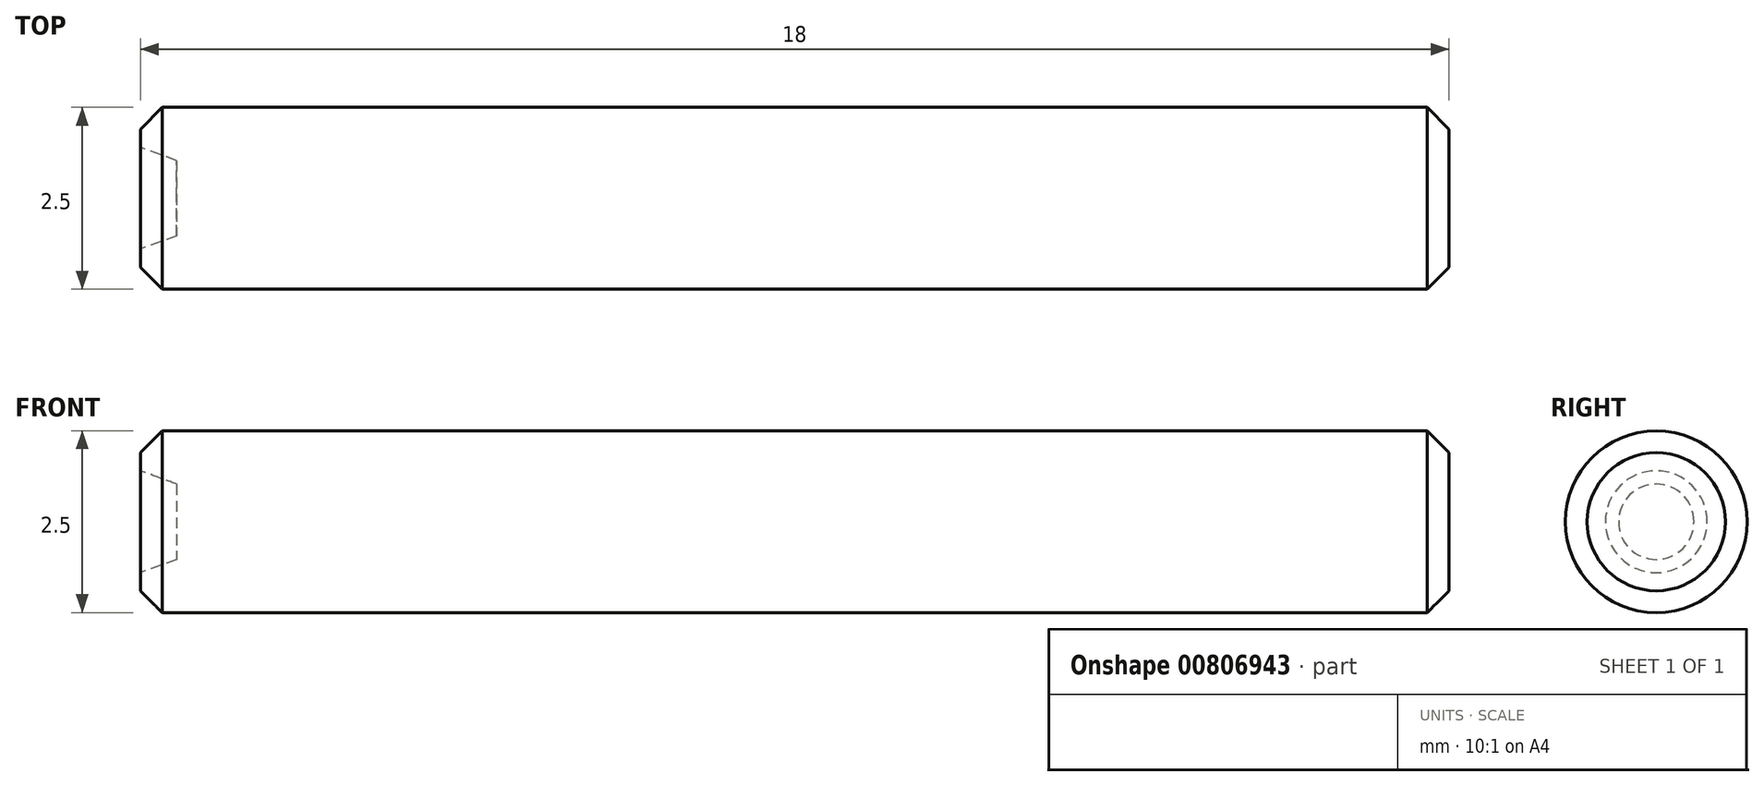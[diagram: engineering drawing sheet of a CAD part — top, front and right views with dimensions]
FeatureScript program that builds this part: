
annotation { "Feature Type Name" : "Feature", "Feature Type Description" : "" }
export const myFeature = defineFeature(function(context is Context, id is Id, definition is map)
    precondition{}
    {
        {
            var Q0;
            Q0=qCreatedBy(makeId("Right.planeOp"),FACE);
            var sketch = newSketch(context, id + "F0", { "sketchPlane" : qUnion([Q0])});
            skCircle(sketch, "E0", {"center": v(0, 0) * mm, "radius": 1.25 * mm});
            skSolve(sketch);
        }
        {
            var Q0;
            Q0=qSketchRegion(id+"F0",true);
            extrude(context, id + "F1", {"entities" : qUnion([Q0]), "endBound" : BoundingType.SYMMETRIC, "depth" : 18 * mm, "offsetDistance" : 25 * mm});
        }
        {
            var Q0;
            Q0=makeQuery(id+"F1.opExtrude","CAP_EDGE",EDGE,{"disambiguationData":[OSD([sQuery(id+"F0.wireOp",EDGE,"E0")])],"isStart":true});
            var Q1;
            Q1=makeQuery(id+"F1.opExtrude","CAP_EDGE",EDGE,{"disambiguationData":[OSD([sQuery(id+"F0.wireOp",EDGE,"E0")])],"isStart":false});
            chamfer(context, id + "F2", {"entities" : qUnion([Q0, Q1]), "width" : 0.3 * mm, "tangentPropagation" : true});
        }
        {
            var Q0;
            Q0=makeQuery(id+"F1.opExtrude","CAP_FACE",FACE,{"disambiguationData":[OSD([sQuery(id+"F0.wireOp",EDGE,"E0")])],"isStart":true});
            var sketch = newSketch(context, id + "F3", { "sketchPlane" : qUnion([Q0])});
            skCircle(sketch, "E1", {"center": v(0, 0) * mm, "radius": 0.7 * mm});
            skSolve(sketch);
        }
        {
            var Q0;
            Q0=qSketchRegion(id+"F3",true);
            extrude(context, id + "F4", {"entities" : qUnion([Q0]), "operationType" : NewBodyOperationType.REMOVE, "oppositeDirection" : true, "depth" : 0.5 * mm, "offsetDistance" : 25 * mm, "hasDraft" : true, "draftAngle" : 20 * degree, "draftPullDirection" : true});
        }
    });
